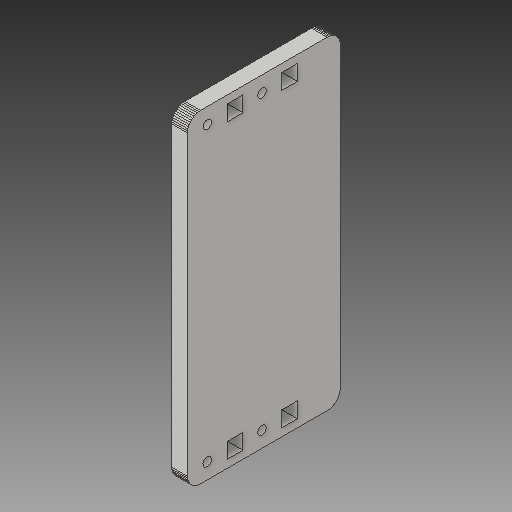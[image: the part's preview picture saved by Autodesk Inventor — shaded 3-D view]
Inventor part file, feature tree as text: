
AUTODESK INVENTOR PART (.ipt)
format: ipt  version: 2017 (Build 210142000, 142)  size: 342,528 bytes
history: native  units: mm
features: other x6, sketch x2, hole x1, reference x1
ambient origin geometry x8: Origin, YZ Plane, XZ Plane, XY Plane, X Axis, Y Axis, Z Axis, Center Point
bodies: Solid1 (feature_tree)
feature tree (10):
  other  "X Axis Brace.ipt"
  hole  "Hole1"  [1 undecoded]
  other  "Solid1::X Axis Brace.ipt"
  other  "TaggingFeature1"
  sketch  "Sketch1"  dims[d0=10.0mm]
  sketch  "Sketch2"  dims[d1=3.3mm d2=6.0mm d3=4.0mm d4=2.0mm d5=90.0deg d6=8.0mm d7=20.594885mm]
  reference  "Reference1"
  parser-record x1  (decoder bookkeeping rows leaked as tree rows — omitted from the tree; the rows remain in map.json)
  other  "Assembly33.iam"
  other  "X Axis Brace:1"
note: 1 required parameter value undecoded (feature->parameter linkage not recoverable at this tier; creation-order binding heuristic only, values carry confidence <= 0.55)
note: 1 file-system path scrubbed to <path> (originals preserved in map.json)
